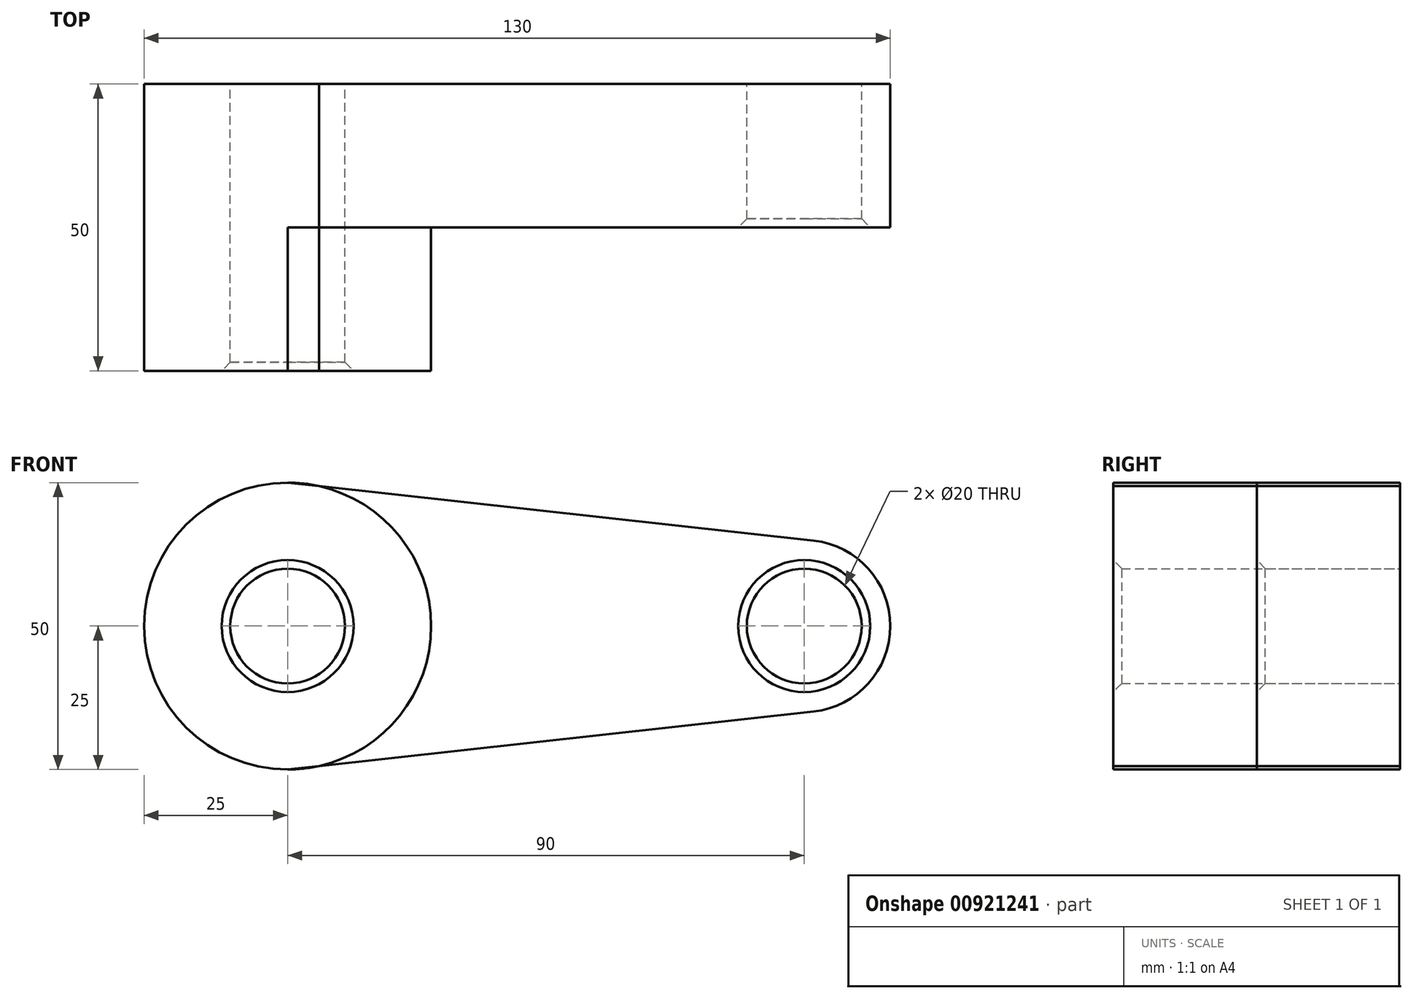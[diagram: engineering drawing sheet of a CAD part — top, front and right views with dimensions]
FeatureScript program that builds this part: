
annotation { "Feature Type Name" : "Feature", "Feature Type Description" : "" }
export const myFeature = defineFeature(function(context is Context, id is Id, definition is map)
    precondition{}
    {
        {
            var Q0;
            Q0=qCreatedBy(makeId("Front.planeOp"),FACE);
            var sketch = newSketch(context, id + "F0", { "sketchPlane" : qUnion([Q0])});
            skCircle(sketch, "E0", {"center": v(0, 0) * mm, "radius": 25 * mm});
            skCircle(sketch, "E1", {"center": v(90, 0) * mm, "radius": 15 * mm});
            skLineSegment(sketch, "E2", {"start": v(0, 25) * mm, "end": v(91.64, 14.9) * mm});
            skLineSegment(sketch, "E3", {"start": v(0, -25) * mm, "end": v(91.64, -14.9) * mm});
            skCircle(sketch, "E4", {"center": v(0, 0) * mm, "radius": 10 * mm});
            skCircle(sketch, "E5", {"center": v(90, 0) * mm, "radius": 10 * mm});
            skSolve(sketch);
        }
        {
            var Q0;
            Q0 = qSketchRegion(id + "F0", true);
            extrude(context, id + "F1", {"entities" : qUnion([Q0]), "depth" : 25 * mm, "offsetDistance" : 25.4 * mm});
        }
        {
            var Q0;
            Q0=makeQuery(id+"F0.imprint","IMPRINT",FACE,{"disambiguationData":[TD([[makeQuery(id+"F0.imprint","IMPRINT",EDGE,{"derivedFrom":sQuery(id+"F0.wireOp",EDGE,"E4")}),-1.0]])]});
            extrude(context, id + "F2", {"entities" : qUnion([Q0]), "operationType" : NewBodyOperationType.ADD, "depth" : 50 * mm, "offsetDistance" : 25.4 * mm});
        }
        {
            var Q0;
            Q0=makeQuery(id+"F1.opExtrude","CAP_EDGE",EDGE,{"disambiguationData":[OSD([sQuery(id+"F0.wireOp",EDGE,"E5")])],"isStart":false});
            var Q1;
            Q1=makeQuery(id+"F2.opExtrude","CAP_EDGE",EDGE,{"disambiguationData":[OSD([sQuery(id+"F0.wireOp",EDGE,"E4")])],"isStart":false});
            var Q2;
            {var subQ0=sQuery(id+"F0.wireOp",EDGE,"E0");Q2=makeQuery(id+"F2.opExtrude","CAP_EDGE",EDGE,{"disambiguationData":[OSD([subQ0]),TDD([makeQuery(id+"F0.imprint","IMPRINT",EDGE,{"disambiguationData":[TD([[makeQuery(id+"F0.imprint","INTERSECT",VERTEX,{"disambiguationData":[OD(1.0)],"derivedFrom":[subQ0,sQuery(id+"F0.wireOp",EDGE,"E2")]}),1.0]])],"derivedFrom":subQ0})])],"isStart":false});}
            var Q3;
            {var subQ0=sQuery(id+"F0.wireOp",EDGE,"E0");Q3=makeQuery(id+"F2.opExtrude","CAP_EDGE",EDGE,{"disambiguationData":[OSD([subQ0]),TDD([makeQuery(id+"F0.imprint","IMPRINT",EDGE,{"disambiguationData":[TD([[makeQuery(id+"F0.imprint","INTERSECT",VERTEX,{"disambiguationData":[OD(0.0)],"derivedFrom":[subQ0,sQuery(id+"F0.wireOp",EDGE,"E2")]}),-1.0]])],"derivedFrom":subQ0})])],"isStart":false});}
            chamfer(context, id + "F3", {"entities" : qUnion([Q0, Q1, Q2, Q3]), "width" : 1.5 * mm, "tangentPropagation" : true});
        }
    });
